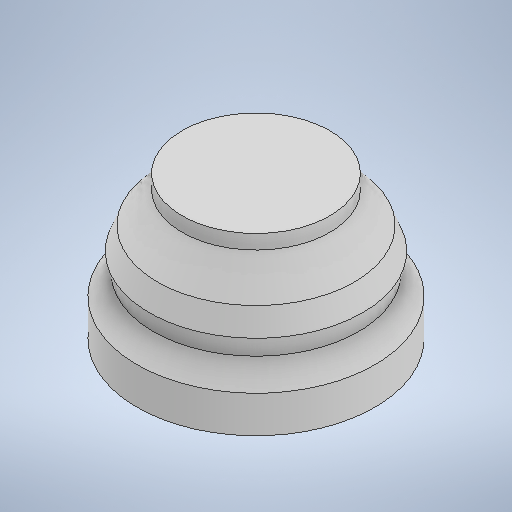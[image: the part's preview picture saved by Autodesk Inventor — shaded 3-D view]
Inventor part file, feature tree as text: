
AUTODESK INVENTOR PART (.ipt)
format: ipt  version: 2025.1 (Build 291241000, 241)  size: 297,984 bytes
history: native  units: mm
features: other x2, revolve x1, sketch x1
ambient origin geometry x8: Origin, YZ Plane, XZ Plane, XY Plane, X Axis, Y Axis, Z Axis, Center Point
bodies: Body1 (feature_tree)
feature tree (4):
  other  "Sólido1"
  revolve  "Revolución1"  [1 undecoded]
  sketch  "Boceto2"  dims[d16=90.0deg d18=23.0mm]
  other  "Imagen2"
note: 1 required parameter value undecoded (feature->parameter linkage not recoverable at this tier; creation-order binding heuristic only, values carry confidence <= 0.55)
